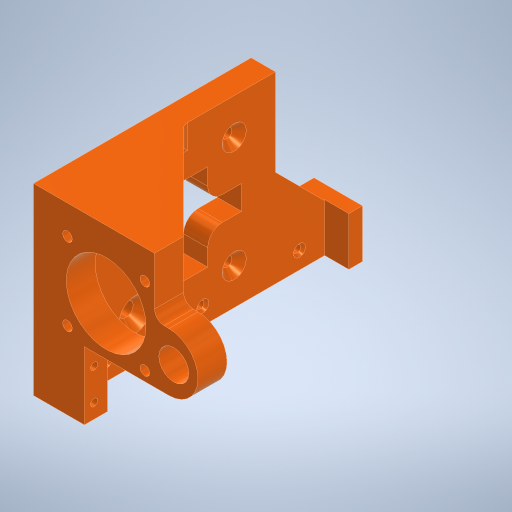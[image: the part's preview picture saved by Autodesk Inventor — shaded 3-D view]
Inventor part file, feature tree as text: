
AUTODESK INVENTOR PART (.ipt)
format: ipt  version: 2024.1 (Build 281209000, 209)  size: 476,672 bytes
history: native  units: in
note: dims shown in document units (in); Inventor stores cm internally (conversion verified against a paired STEP export)
features: extrude x18, sketch x18, chamfer x5, fillet x4
ambient origin geometry x8: Origin, YZ Plane, XZ Plane, XY Plane, X Axis, Y Axis, Z Axis, Center Point
bodies: Solid1 (feature_tree)
feature tree (45):
  extrude  "Extrusion1"  Depth=1.4961in
  extrude  "Extrusion2"  Depth=0.9449in
  extrude  "Extrusion3"  Depth=0.7874in TaperAngle=0.0deg
  extrude  "Extrusion4"  Depth=0.3937in
  extrude  "Extrusion5"  Depth=0.0787in
  fillet  "Fillet1"  Radius=0.0787in
  extrude  "Extrusion6"  Depth=0.0787in
  extrude  "Extrusion7"  Depth=0.315in
  chamfer  "Chamfer1"  [1 undecoded]
  chamfer  "Chamfer2"  Distance=0.7874in
  extrude  "Extrusion8"  Depth=0.0787in
  chamfer  "Chamfer3"  [1 undecoded]
  extrude  "Extrusion9"  Depth=0.1181in
  chamfer  "Chamfer4"  Distance=0.1181in
  extrude  "Extrusion10"  Depth=0.1575in
  extrude  "Extrusion15"  Depth=0.0787in
  extrude  "Extrusion16"  Depth=0.0787in
  extrude  "Extrusion17"  Depth=0.1575in
  extrude  "Extrusion18"  TaperAngle=0.0deg  [1 undecoded]
  extrude  "Extrusion19"  Depth=0.0591in TaperAngle=45.0deg
  chamfer  "Chamfer5"  Distance=0.0787in Angle=45.0deg
  extrude  "Extrusion20"  Depth=1.1024in
  extrude  "Extrusion21"  Depth=0.3937in
  fillet  "Fillet3"  [1 undecoded]
  extrude  "Extrusion22"  Depth=0.3937in TaperAngle=45.0deg
  fillet  "Fillet5"  Radius=0.0787in
  fillet  "Fillet6"  Radius=0.0787in
  sketch  "Sketch1"  dims[d0=1.4961in d1=2.1654in]
  sketch  "Sketch2"  dims[d2=0.1969in d3=0.0in d4=0.9449in]
  sketch  "Sketch3"  dims[d5=0.2362in d6=0.7874in d7=0.0in]
  sketch  "Sketch4"  dims[d8=0.6496in d9=0.3937in]
  sketch  "Sketch5"  dims[d10=0.3937in d11=0.0787in d12=0.0787in]
  sketch  "Sketch6"  dims[d13=0.0787in d14=0.0787in]
  sketch  "Sketch7"  dims[d15=0.315in d16=0.315in]
  sketch  "Sketch8"  dims[d17=0.315in]
  sketch  "Sketch9"  dims[d18=0.315in]
  sketch  "Sketch10"  dims[d19=0.315in]
  sketch  "Sketch15"  dims[d20=0.315in]
  sketch  "Sketch16"  dims[d21=0.315in]
  sketch  "Sketch17"  dims[d22=0.315in d23=0.0in d24=0.0in]
  sketch  "Sketch18"  dims[d25=0.1181in d26=0.7874in d27=0.0in]
  sketch  "Sketch19"  dims[d28=0.0in d29=0.0in d30=0.0787in]
  sketch  "Sketch20"  dims[d31=0.0787in]
  sketch  "Sketch21"  dims[d32=0.7087in]
  sketch  "Sketch22"  dims[d33=1.378in d34=0.0in d35=0.0in d36=0.1181in d37=0.1181in d38=0.1575in d39=0.4331in d40=0.4331in d41=0.1575in d42=0.0in d43=0.0in d44=0.0591in d45=0.0787in d46=45.0deg d47=0.0748in d48=0.0787in d49=45.0deg d50=1.1024in d51=0.3937in d52=0.0in d53=0.0in d54=0.3937in d55=0.0787in d56=45.0deg d57=0.0787in d58=0.0787in d59=0.2953in d60=0.7283in d61=0.2953in d62=0.7283in d63=0.0in d64=0.0in d65=0.0591in d66=0.0787in d67=45.0deg d68=0.0591in d69=0.0591in d70=0.0591in d71=0.1378in d72=0.1969in d73=0.1378in d74=0.7874in d76=0.1378in d77=0.0in d78=0.0in d95=0.7874in d96=0.1181in d97=0.3937in d98=0.2165in d99=0.0in d100=0.1102in d101=0.1969in d102=0.0in d103=0.189in d104=0.2165in d105=0.0in d106=0.0591in d107=0.0591in d108=0.2559in d109=0.1181in d110=0.0787in d111=0.0787in d112=0.0in d113=0.0in d114=0.1969in d115=0.3937in d116=0.3937in d117=0.5512in d118=0.0in d119=0.0in d120=0.0197in d121=0.0787in d122=45.0deg d123=0.4724in d124=0.3543in d125=0.0in d126=0.2441in d127=0.2362in d128=0.1969in d129=0.0in d130=0.0in d132=0.2362in d134=0.1969in d135=0.2559in d136=0.2756in d137=0.0in d138=0.0in d139=0.1181in d152=0.0787in]
note: 4 required parameter values undecoded (feature->parameter linkage not recoverable at this tier; creation-order binding heuristic only, values carry confidence <= 0.55)
